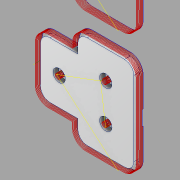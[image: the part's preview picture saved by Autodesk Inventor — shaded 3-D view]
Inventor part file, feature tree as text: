
AUTODESK INVENTOR PART (.ipt)
format: ipt  version: 2021.3 (Build 253353000, 353)  size: 193,024 bytes
history: native  units: in
note: dims shown in document units (in); Inventor stores cm internally (conversion verified against a paired STEP export)
features: other x9, reference x7, extrude x1, fillet x1
ambient origin geometry x8: Origin, YZ Plane, XZ Plane, XY Plane, X Axis, Y Axis, Z Axis, Center Point
bodies: Body1 (feature_tree)
feature tree (18):
  other  "ソリッド1"
  other  "作業平面1"
  extrude  "押し出し1"  Depth=0.7874in
  fillet  "フィレット1"  Radius=1.1811in
  reference  "参照5"
  reference  "参照6"
  reference  "参照7"
  reference  "参照8"
  reference  "参照9"
  reference  "参照10"
  reference  "参照11"
  other  "<userpath>\workspace\beetle_inventor_model\suspension\bogie.iam"
  other  "bogie.iam"
  other  "wheel_with_mounts:2"
  other  "wheel_mount:2"
  other  "wheel_mount"
  other  "AFS-2040-4-130:1"
  other  "AFS-2040-4-50:1"
